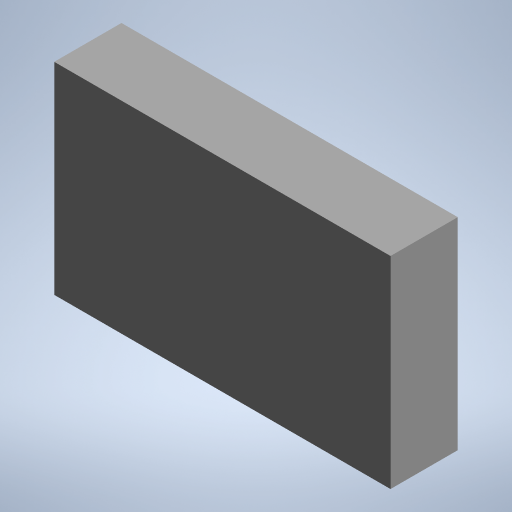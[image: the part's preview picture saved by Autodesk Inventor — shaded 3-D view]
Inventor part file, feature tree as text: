
AUTODESK INVENTOR PART (.ipt)
format: ipt  version: 2024 (Build 280153020, 153B)  size: 212,992 bytes
history: native  units: mm (DEFAULTED — no unit token found)
features: other x6, sketch x2, extrude x1
bodies: Body1 (feature_tree)
feature tree (9):
  other  "솔리드1"
  extrude  "돌출1"  Depth=10.0mm TaperAngle=0.0deg
  other  "엠보싱1"
  other  "YZ 평면"
  other  "XZ 평면"
  other  "XY 평면"
  other  "중심점"
  sketch  "스케치1"
  sketch  "스케치2"
